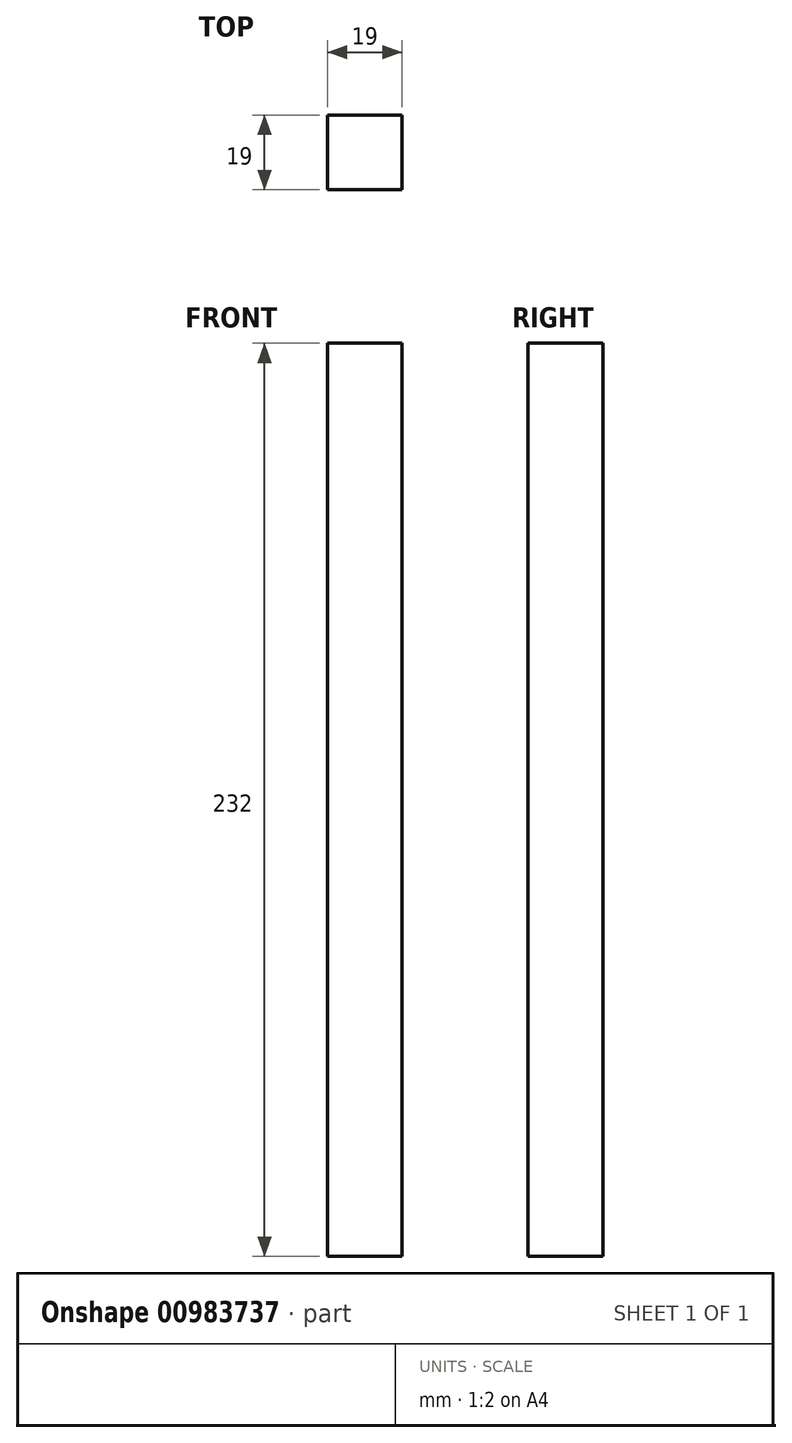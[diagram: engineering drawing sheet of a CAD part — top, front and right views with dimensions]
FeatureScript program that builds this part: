
annotation { "Feature Type Name" : "Feature", "Feature Type Description" : "" }
export const myFeature = defineFeature(function(context is Context, id is Id, definition is map)
    precondition{}
    {
        {
            var Q0;
            Q0=qCreatedBy(makeId("Front.planeOp"),FACE);
            var sketch = newSketch(context, id + "F0", { "sketchPlane" : qUnion([Q0])});
            skLineSegment(sketch, "E0.bottom", {"start": v(-10.73, 232) * mm, "end": v(8.27, 232) * mm});
            skLineSegment(sketch, "E0.top", {"start": v(-10.73, 0) * mm, "end": v(8.27, 0) * mm});
            skLineSegment(sketch, "E0.left", {"start": v(-10.73, 232) * mm, "end": v(-10.73, 0) * mm});
            skLineSegment(sketch, "E0.right", {"start": v(8.27, 232) * mm, "end": v(8.27, 0) * mm});
            skSolve(sketch);
        }
        {
            var Q0;
            Q0 = qSketchRegion(id + "F0", true);
            var Q1;
            Q1=makeQuery(id+"F0.imprint","IMPRINT",FACE,{"disambiguationData":[TD([[makeQuery(id+"F0.imprint","IMPRINT",EDGE,{"derivedFrom":sQuery(id+"F0.wireOp",EDGE,"E0.bottom")}),-1.0]])]});
            extrude(context, id + "F1", {"entities" : qUnion([Q0, Q1]), "depth" : 19 * mm, "offsetDistance" : 25.4 * mm});
        }
        {
            var Q0;
            Q0 = qSketchRegion(id + "F0", true);
            extrude(context, id + "F2", {"entities" : qUnion([Q0]), "operationType" : NewBodyOperationType.ADD, "depth" : 19 * mm, "offsetDistance" : 25.4 * mm});
        }
    });
